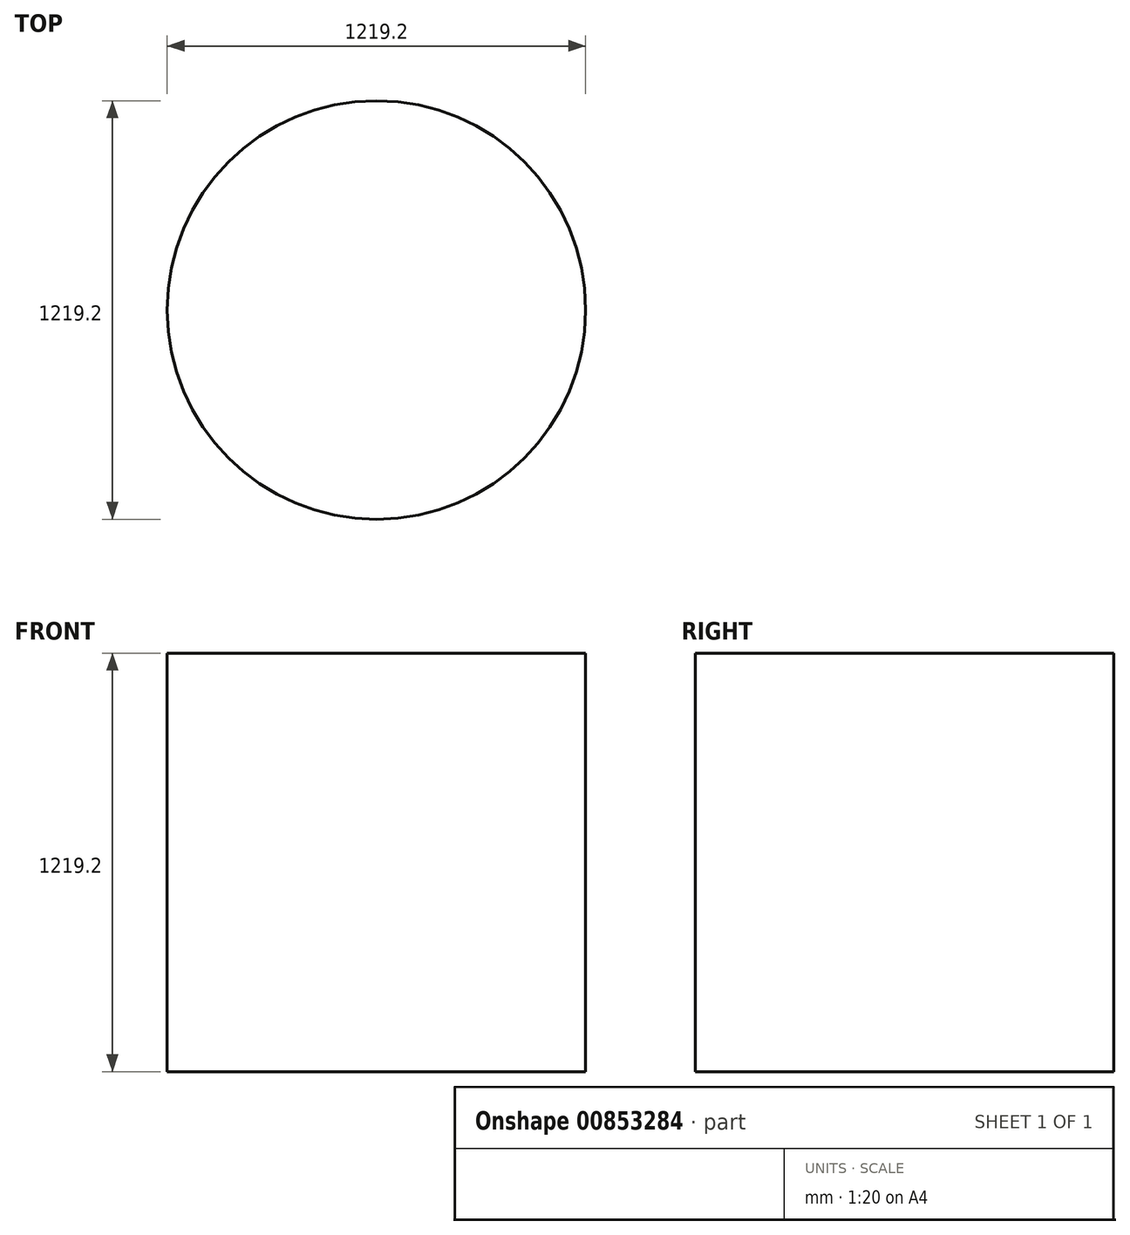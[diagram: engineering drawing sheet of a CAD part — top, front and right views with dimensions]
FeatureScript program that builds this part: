
annotation { "Feature Type Name" : "Feature", "Feature Type Description" : "" }
export const myFeature = defineFeature(function(context is Context, id is Id, definition is map)
    precondition{}
    {
        {
            var Q0;
            Q0=qCreatedBy(makeId("Top.planeOp"),FACE);
            var sketch = newSketch(context, id + "F0", { "sketchPlane" : qUnion([Q0])});
            skCircle(sketch, "E0", {"center": v(0, 0) * mm, "radius": 609.6 * mm});
            skSolve(sketch);
        }
        {
            var Q0;
            Q0 = qSketchRegion(id + "F0", true);
            extrude(context, id + "F1", {"entities" : qUnion([Q0]), "depth" : 1219.2 * mm, "offsetDistance" : 25.4 * mm});
        }
    });
